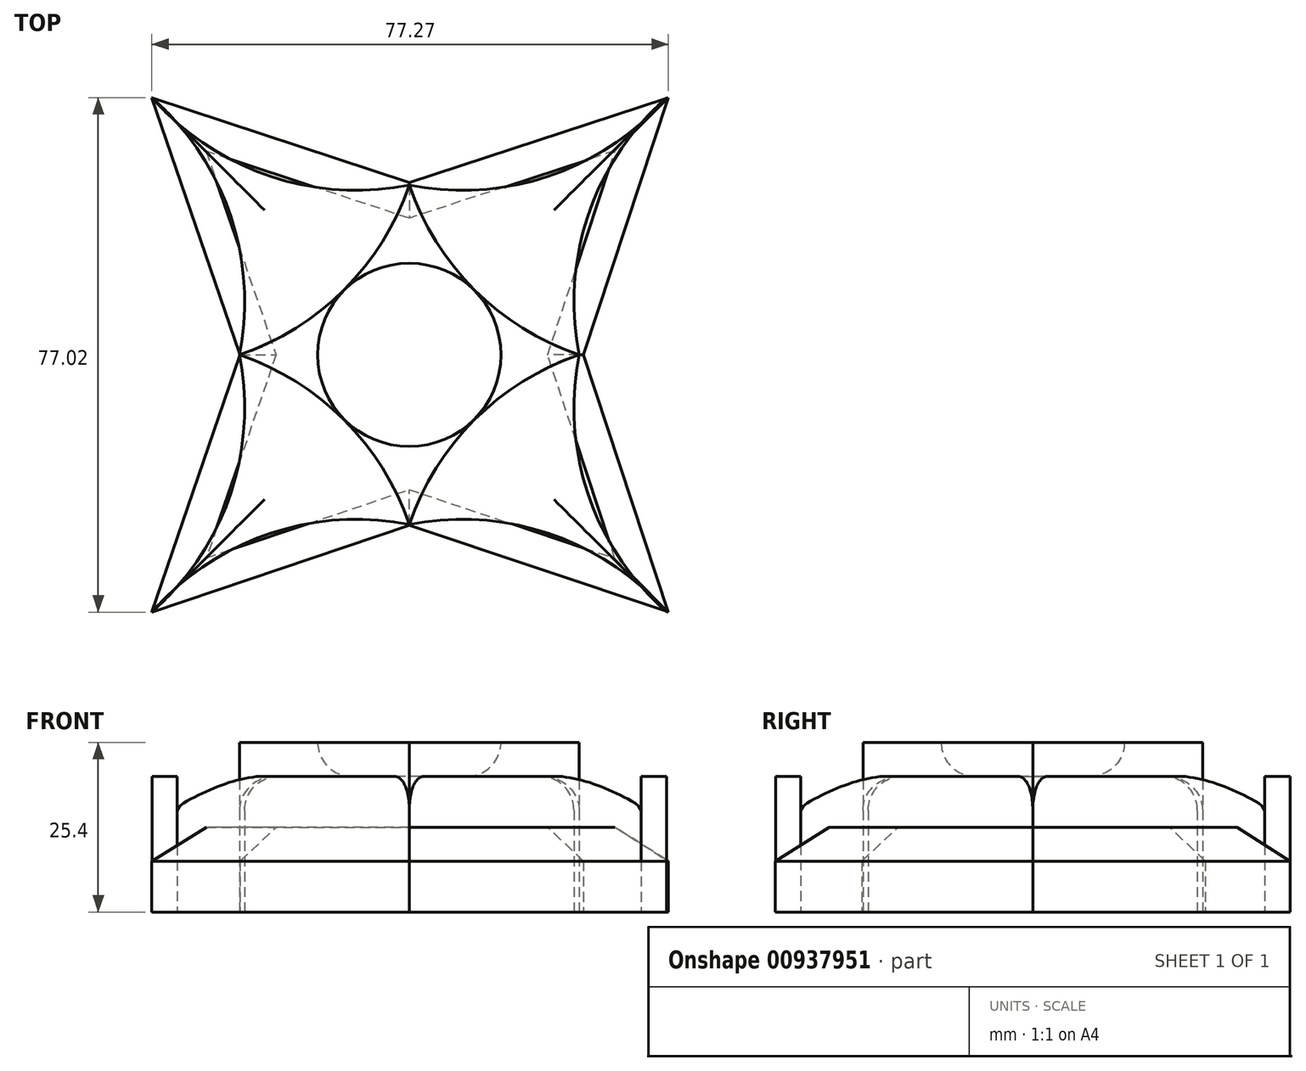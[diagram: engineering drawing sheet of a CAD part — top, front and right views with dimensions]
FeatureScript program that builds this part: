
annotation { "Feature Type Name" : "Feature", "Feature Type Description" : "" }
export const myFeature = defineFeature(function(context is Context, id is Id, definition is map)
    precondition{}
    {
        {
            var Q0;
            Q0=qCreatedBy(makeId("Top.planeOp"),FACE);
            var sketch = newSketch(context, id + "F0", { "sketchPlane" : qUnion([Q0])});
            skCircle(sketch, "E0", {"center": v(0, 0) * mm, "radius": 13.7 * mm});
            skLineSegment(sketch, "E1", {"start": v(0, 0) * mm, "end": v(-25.4, 0) * mm});
            skLineSegment(sketch, "E2", {"start": v(0, 0) * mm, "end": v(0, -25.4) * mm});
            skLineSegment(sketch, "E3", {"start": v(0, 0) * mm, "end": v(0, 25.4) * mm});
            skLineSegment(sketch, "E4", {"start": v(0, 0) * mm, "end": v(25.4, 0) * mm});
            skArc(sketch, "E5", {"start": v(0, 25.4) * mm, "mid": v(9.74, 9.74) * mm, "end": v(25.4, 0) * mm});
            skArc(sketch, "E6", {"start": v(25.4, 0) * mm, "mid": v(9.74, -9.74) * mm, "end": v(0, -25.4) * mm});
            skArc(sketch, "E7", {"start": v(0, -25.4) * mm, "mid": v(-9.74, -9.74) * mm, "end": v(-25.4, 0) * mm});
            skArc(sketch, "E8", {"start": v(-25.4, 0) * mm, "mid": v(-9.74, 9.74) * mm, "end": v(0, 25.4) * mm});
            skSolve(sketch);
        }
        {
            var Q0;
            Q0=qCreatedBy(makeId("Top.planeOp"),FACE);
            var sketch = newSketch(context, id + "F1", { "sketchPlane" : qUnion([Q0])});
            skArc(sketch, "E9", {"start": v(38.48, 38.48) * mm, "mid": v(26.78, 21) * mm, "end": v(25.4, 0) * mm});
            skArc(sketch, "E10", {"start": v(0, 25.4) * mm, "mid": v(21, 26.78) * mm, "end": v(38.48, 38.48) * mm});
            skArc(sketch, "E11", {"start": v(25.4, 0) * mm, "mid": v(26.78, -21) * mm, "end": v(38.48, -38.48) * mm});
            skArc(sketch, "E12", {"start": v(38.48, -38.48) * mm, "mid": v(21, -26.78) * mm, "end": v(0, -25.4) * mm});
            skArc(sketch, "E13", {"start": v(0, -25.4) * mm, "mid": v(-21, -26.78) * mm, "end": v(-38.48, -38.48) * mm});
            skArc(sketch, "E14", {"start": v(-38.48, -38.48) * mm, "mid": v(-26.78, -21) * mm, "end": v(-25.4, 0) * mm});
            skArc(sketch, "E15", {"start": v(-25.4, 0) * mm, "mid": v(-26.78, 21) * mm, "end": v(-38.48, 38.48) * mm});
            skArc(sketch, "E16", {"start": v(-38.48, 38.48) * mm, "mid": v(-21, 26.78) * mm, "end": v(0, 25.4) * mm});
            skSolve(sketch);
        }
        {
            var Q0;
            Q0=qCreatedBy(makeId("Top.planeOp"),FACE);
            var sketch = newSketch(context, id + "F2", { "sketchPlane" : qUnion([Q0])});
            skLineSegment(sketch, "E17", {"start": v(-38.5, 38.5) * mm, "end": v(0, 25.8) * mm});
            skLineSegment(sketch, "E18", {"start": v(0, 25.8) * mm, "end": v(38.76, 38.5) * mm});
            skLineSegment(sketch, "E19", {"start": v(38.76, 38.5) * mm, "end": v(26.05, 0) * mm});
            skLineSegment(sketch, "E20", {"start": v(26.05, 0) * mm, "end": v(38.76, -38.5) * mm});
            skLineSegment(sketch, "E21", {"start": v(38.76, -38.5) * mm, "end": v(0, -25.55) * mm});
            skLineSegment(sketch, "E22", {"start": v(0, -25.55) * mm, "end": v(-38.5, -38.5) * mm});
            skLineSegment(sketch, "E23", {"start": v(-38.5, -38.5) * mm, "end": v(-25.3, 0) * mm});
            skLineSegment(sketch, "E24", {"start": v(-25.3, 0) * mm, "end": v(-38.5, 38.5) * mm});
            skSolve(sketch);
        }
        {
            var Q0;
            Q0 = qSketchRegion(id + "F0", true);
            extrude(context, id + "F3", {"entities" : qUnion([Q0]), "depth" : 25.4 * mm, "offsetDistance" : 25.4 * mm});
        }
        {
            var Q0;
            Q0 = qSketchRegion(id + "F1", true);
            extrude(context, id + "F4", {"entities" : qUnion([Q0]), "operationType" : NewBodyOperationType.ADD, "depth" : 20.32 * mm, "offsetDistance" : 25.4 * mm});
        }
        {
            var Q0;
            Q0 = qSketchRegion(id + "F2", true);
            extrude(context, id + "F5", {"entities" : qUnion([Q0]), "depth" : 12.7 * mm, "offsetDistance" : 25.4 * mm});
        }
        {
            var Q0;
            {var subQ0=sQuery(id+"F1.wireOp",EDGE,"E12");Q0=makeQuery(id+"F4.opExtrude","CAP_EDGE",EDGE,{"disambiguationData":[OSD([subQ0]),TDD([makeQuery(id+"F1.imprint","IMPRINT",EDGE,{"disambiguationData":[TD([[makeQuery(id+"F1.imprint","INTERSECT",VERTEX,{"derivedFrom":[subQ0,sQuery(id+"F1.wireOp",EDGE,"E13")]}),1.0]])],"derivedFrom":subQ0})])],"isStart":false});}
            var Q1;
            {var subQ0=sQuery(id+"F1.wireOp",EDGE,"E13");Q1=makeQuery(id+"F4.opExtrude","CAP_EDGE",EDGE,{"disambiguationData":[OSD([subQ0]),TDD([makeQuery(id+"F1.imprint","IMPRINT",EDGE,{"disambiguationData":[TD([[makeQuery(id+"F1.imprint","INTERSECT",VERTEX,{"derivedFrom":[sQuery(id+"F1.wireOp",EDGE,"E12"),subQ0]}),-1.0]])],"derivedFrom":subQ0})])],"isStart":false});}
            var Q2;
            {var subQ0=sQuery(id+"F1.wireOp",EDGE,"E11");Q2=makeQuery(id+"F4.opExtrude","CAP_EDGE",EDGE,{"disambiguationData":[OSD([subQ0]),TDD([makeQuery(id+"F1.imprint","IMPRINT",EDGE,{"disambiguationData":[TD([[makeQuery(id+"F1.imprint","INTERSECT",VERTEX,{"derivedFrom":[sQuery(id+"F1.wireOp",EDGE,"E9"),subQ0]}),-1.0]])],"derivedFrom":subQ0})])],"isStart":false});}
            var Q3;
            {var subQ0=sQuery(id+"F1.wireOp",EDGE,"E9");Q3=makeQuery(id+"F4.opExtrude","CAP_EDGE",EDGE,{"disambiguationData":[OSD([subQ0]),TDD([makeQuery(id+"F1.imprint","IMPRINT",EDGE,{"disambiguationData":[TD([[makeQuery(id+"F1.imprint","INTERSECT",VERTEX,{"derivedFrom":[subQ0,sQuery(id+"F1.wireOp",EDGE,"E11")]}),1.0]])],"derivedFrom":subQ0})])],"isStart":false});}
            var Q4;
            {var subQ0=sQuery(id+"F1.wireOp",EDGE,"E10");Q4=makeQuery(id+"F4.opExtrude","CAP_EDGE",EDGE,{"disambiguationData":[OSD([subQ0]),TDD([makeQuery(id+"F1.imprint","IMPRINT",EDGE,{"disambiguationData":[TD([[makeQuery(id+"F1.imprint","INTERSECT",VERTEX,{"derivedFrom":[subQ0,sQuery(id+"F1.wireOp",EDGE,"E16")]}),-1.0]])],"derivedFrom":subQ0})])],"isStart":false});}
            var Q5;
            {var subQ0=sQuery(id+"F1.wireOp",EDGE,"E16");Q5=makeQuery(id+"F4.opExtrude","CAP_EDGE",EDGE,{"disambiguationData":[OSD([subQ0]),TDD([makeQuery(id+"F1.imprint","IMPRINT",EDGE,{"disambiguationData":[TD([[makeQuery(id+"F1.imprint","INTERSECT",VERTEX,{"derivedFrom":[sQuery(id+"F1.wireOp",EDGE,"E10"),subQ0]}),1.0]])],"derivedFrom":subQ0})])],"isStart":false});}
            var Q6;
            {var subQ0=sQuery(id+"F1.wireOp",EDGE,"E15");Q6=makeQuery(id+"F4.opExtrude","CAP_EDGE",EDGE,{"disambiguationData":[OSD([subQ0]),TDD([makeQuery(id+"F1.imprint","IMPRINT",EDGE,{"disambiguationData":[TD([[makeQuery(id+"F1.imprint","INTERSECT",VERTEX,{"derivedFrom":[sQuery(id+"F1.wireOp",EDGE,"E14"),subQ0]}),-1.0]])],"derivedFrom":subQ0})])],"isStart":false});}
            var Q7;
            {var subQ0=sQuery(id+"F1.wireOp",EDGE,"E14");Q7=makeQuery(id+"F4.opExtrude","CAP_EDGE",EDGE,{"disambiguationData":[OSD([subQ0]),TDD([makeQuery(id+"F1.imprint","IMPRINT",EDGE,{"disambiguationData":[TD([[makeQuery(id+"F1.imprint","INTERSECT",VERTEX,{"derivedFrom":[subQ0,sQuery(id+"F1.wireOp",EDGE,"E15")]}),1.0]])],"derivedFrom":subQ0})])],"isStart":false});}
            fillet(context, id + "F6", {"entities" : qUnion([Q0, Q1, Q2, Q3, Q4, Q5, Q6, Q7]), "tangentPropagation" : true, "radius" : 5.08 * mm, "defaultsChanged" : false, "vertexSettings" : [], "allowEdgeOverflow" : false});
        }
        {
            var Q0;
            Q0=makeQuery(id+"F5.opExtrude","CAP_EDGE",EDGE,{"disambiguationData":[OSD([sQuery(id+"F2.wireOp",EDGE,"E22")])],"isStart":false});
            var Q1;
            Q1=makeQuery(id+"F5.opExtrude","CAP_EDGE",EDGE,{"disambiguationData":[OSD([sQuery(id+"F2.wireOp",EDGE,"E21")])],"isStart":false});
            var Q2;
            Q2=makeQuery(id+"F5.opExtrude","CAP_EDGE",EDGE,{"disambiguationData":[OSD([sQuery(id+"F2.wireOp",EDGE,"E20")])],"isStart":false});
            var Q3;
            Q3=makeQuery(id+"F5.opExtrude","CAP_EDGE",EDGE,{"disambiguationData":[OSD([sQuery(id+"F2.wireOp",EDGE,"E19")])],"isStart":false});
            var Q4;
            Q4=makeQuery(id+"F5.opExtrude","CAP_EDGE",EDGE,{"disambiguationData":[OSD([sQuery(id+"F2.wireOp",EDGE,"E18")])],"isStart":false});
            var Q5;
            Q5=makeQuery(id+"F5.opExtrude","CAP_EDGE",EDGE,{"disambiguationData":[OSD([sQuery(id+"F2.wireOp",EDGE,"E17")])],"isStart":false});
            var Q6;
            Q6=makeQuery(id+"F5.opExtrude","CAP_EDGE",EDGE,{"disambiguationData":[OSD([sQuery(id+"F2.wireOp",EDGE,"E24")])],"isStart":false});
            var Q7;
            Q7=makeQuery(id+"F5.opExtrude","CAP_EDGE",EDGE,{"disambiguationData":[OSD([sQuery(id+"F2.wireOp",EDGE,"E23")])],"isStart":false});
            chamfer(context, id + "F7", {"entities" : qUnion([Q0, Q1, Q2, Q3, Q4, Q5, Q6, Q7]), "width" : 5.08 * mm, "tangentPropagation" : true});
        }
        {
            var Q0;
            Q0=makeQuery(id+"F4.boolean.opBoolean","INTERSECT",EDGE,{"derivedFrom":[makeQuery(id+"F3.opExtrude","SWEPT_FACE",FACE,{"disambiguationData":[OSD([sQuery(id+"F0.wireOp",EDGE,"E0")])]}),makeQuery(id+"F4.opExtrude","CAP_FACE",FACE,{"disambiguationData":[OSD([sQuery(id+"F1.wireOp",EDGE,"E9"),sQuery(id+"F1.wireOp",EDGE,"E10"),sQuery(id+"F1.wireOp",EDGE,"E11"),sQuery(id+"F1.wireOp",EDGE,"E12"),sQuery(id+"F1.wireOp",EDGE,"E13"),sQuery(id+"F1.wireOp",EDGE,"E14"),sQuery(id+"F1.wireOp",EDGE,"E15"),sQuery(id+"F1.wireOp",EDGE,"E16")])],"isStart":false})]});
            fillet(context, id + "F8", {"entities" : qUnion([Q0]), "tangentPropagation" : true, "radius" : 5.08 * mm, "defaultsChanged" : false, "vertexSettings" : [], "allowEdgeOverflow" : false});
        }
    });
